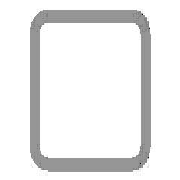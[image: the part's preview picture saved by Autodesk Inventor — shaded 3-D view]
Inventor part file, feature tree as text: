
AUTODESK INVENTOR PART (.ipt)
format: ipt  version: 2024 (Build 280153000, 153)  size: 128,512 bytes
history: native  units: mm (DEFAULTED — no unit token found)
features: other x4, extrude x1, sketch x1, plane x1
ambient origin geometry x8: Origin, YZ Plane, XZ Plane, XY Plane, X Axis, Y Axis, Z Axis, Center Point
bodies: Solid1 (feature_tree)
feature tree (7):
  parser-record x1  (decoder bookkeeping rows leaked as tree rows — omitted from the tree; the rows remain in map.json)
  other  "Driven Length"
  other  "Plano inicial"
  other  "Plano final"
  extrude  "Cuerpo"  TaperAngle=0.0deg  [1 undecoded]
  sketch  "Sketch3"  dims[d3=3000.0mm d4=0.0mm d10=50.8mm d11=50.8mm d12=3.175mm d13=-0.0mm d14=3000.0mm d15=25.4mm d16=25.4mm d17=6.35mm d18=90.0deg d19=3000.0mm]
  plane  "Work Plane3"
note: 1 required parameter value undecoded (feature->parameter linkage not recoverable at this tier; creation-order binding heuristic only, values carry confidence <= 0.55)
